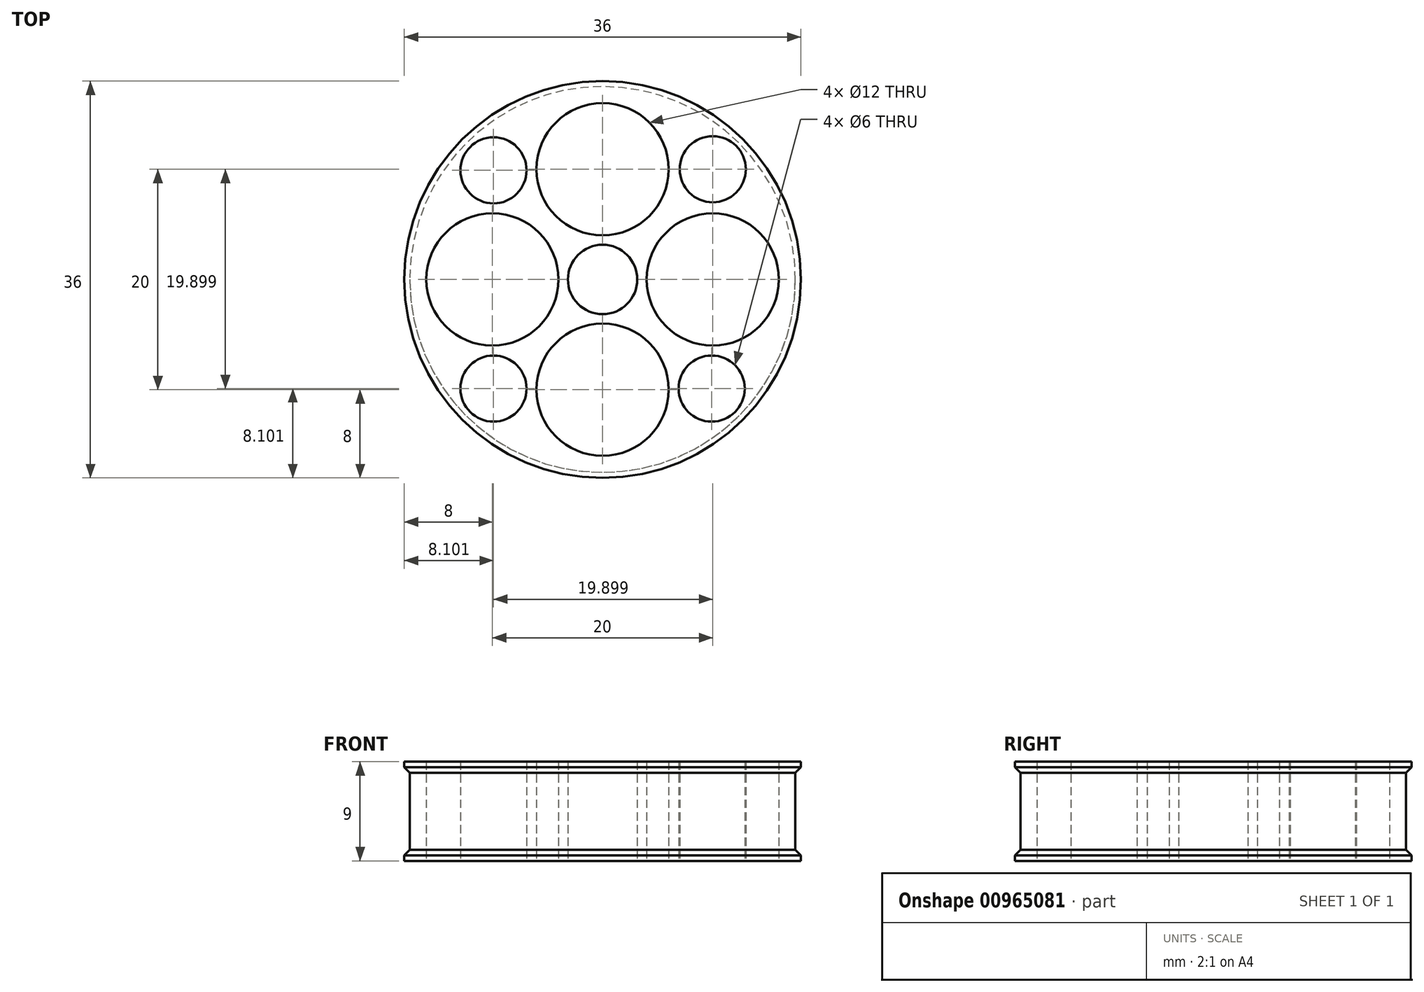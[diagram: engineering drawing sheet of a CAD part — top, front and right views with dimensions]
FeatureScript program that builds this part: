
annotation { "Feature Type Name" : "Feature", "Feature Type Description" : "" }
export const myFeature = defineFeature(function(context is Context, id is Id, definition is map)
    precondition{}
    {
        {
            var Q0;
            Q0=qCreatedBy(makeId("Top.planeOp"),FACE);
            var sketch = newSketch(context, id + "F0", { "sketchPlane" : qUnion([Q0])});
            skCircle(sketch, "E0", {"center": v(0, 0) * mm, "radius": 17.5 * mm});
            skCircle(sketch, "E1", {"center": v(0, 0) * mm, "radius": 3.15 * mm});
            skCircle(sketch, "E2", {"center": v(0, 10) * mm, "radius": 6 * mm});
            skCircle(sketch, "E3", {"center": v(10, 0) * mm, "radius": 6 * mm});
            skCircle(sketch, "E4", {"center": v(0, -10) * mm, "radius": 6 * mm});
            skCircle(sketch, "E5", {"center": v(-10, 0) * mm, "radius": 6 * mm});
            skLineSegment(sketch, "E6", {"start": v(-15.8, 15.8) * mm, "end": v(19.1, -19.1) * mm, "construction": true});
            skLineSegment(sketch, "E7", {"start": v(16.46, 16.46) * mm, "end": v(-16.86, -16.86) * mm, "construction": true});
            skCircle(sketch, "E8", {"center": v(9.9, -9.9) * mm, "radius": 3 * mm});
            skCircle(sketch, "E9", {"center": v(-9.9, -9.9) * mm, "radius": 3 * mm});
            skCircle(sketch, "E10", {"center": v(10, 10) * mm, "radius": 3 * mm});
            skCircle(sketch, "E11", {"center": v(-9.9, 9.9) * mm, "radius": 3 * mm});
            skSolve(sketch);
        }
        {
            var Q0;
            Q0=makeQuery(id+"F0.imprint","IMPRINT",FACE,{"disambiguationData":[TD([[makeQuery(id+"F0.imprint","IMPRINT",EDGE,{"derivedFrom":sQuery(id+"F0.wireOp",EDGE,"E0")}),1.0]])]});
            extrude(context, id + "F1", {"entities" : qUnion([Q0]), "depth" : 7 * mm, "offsetDistance" : 25 * mm});
        }
        {
            var Q0;
            Q0=makeQuery(id+"F1.opExtrude","CAP_FACE",FACE,{"disambiguationData":[OSD([sQuery(id+"F0.wireOp",EDGE,"E0"),sQuery(id+"F0.wireOp",EDGE,"E1"),sQuery(id+"F0.wireOp",EDGE,"E2"),sQuery(id+"F0.wireOp",EDGE,"E3"),sQuery(id+"F0.wireOp",EDGE,"E4"),sQuery(id+"F0.wireOp",EDGE,"E5")])],"isStart":false});
            var sketch = newSketch(context, id + "F2", { "sketchPlane" : qUnion([Q0])});
            skCircle(sketch, "E12", {"center": v(0, 0) * mm, "radius": 18 * mm});
            skSolve(sketch);
        }
        {
            var Q0;
            Q0=makeQuery(id+"F2.imprint","IMPRINT",FACE,{"disambiguationData":[TD([[makeQuery(id+"F2.imprint","IMPRINT",EDGE,{"derivedFrom":sQuery(id+"F2.wireOp",EDGE,"E12")}),1.0]])]});
            var Q1;
            Q1=makeQuery(id+"F2.imprint","IMPRINT",FACE,{"disambiguationData":[TD([[makeQuery(id+"F2.imprint","IMPRINT",EDGE,{"derivedFrom":makeQuery(id+"F1.opExtrude","CAP_EDGE",EDGE,{"disambiguationData":[OSD([sQuery(id+"F0.wireOp",EDGE,"E0")])],"isStart":false})}),1.0]])]});
            extrude(context, id + "F3", {"entities" : qUnion([Q0, Q1]), "operationType" : NewBodyOperationType.ADD, "depth" : 1 * mm, "offsetDistance" : 25 * mm});
        }
        {
            var Q0;
            Q0=makeQuery(id+"F1.opExtrude","CAP_FACE",FACE,{"disambiguationData":[OSD([sQuery(id+"F0.wireOp",EDGE,"E0"),sQuery(id+"F0.wireOp",EDGE,"E1"),sQuery(id+"F0.wireOp",EDGE,"E2"),sQuery(id+"F0.wireOp",EDGE,"E3"),sQuery(id+"F0.wireOp",EDGE,"E4"),sQuery(id+"F0.wireOp",EDGE,"E5")])],"isStart":true});
            var sketch = newSketch(context, id + "F4", { "sketchPlane" : qUnion([Q0])});
            skCircle(sketch, "E13", {"center": v(0, 0) * mm, "radius": 18 * mm});
            skSolve(sketch);
        }
        {
            var Q0;
            Q0=makeQuery(id+"F4.imprint","IMPRINT",FACE,{"disambiguationData":[TD([[makeQuery(id+"F4.imprint","IMPRINT",EDGE,{"derivedFrom":sQuery(id+"F4.wireOp",EDGE,"E13")}),1.0]])]});
            var Q1;
            Q1=makeQuery(id+"F4.imprint","IMPRINT",FACE,{"disambiguationData":[TD([[makeQuery(id+"F4.imprint","IMPRINT",EDGE,{"derivedFrom":makeQuery(id+"F1.opExtrude","CAP_EDGE",EDGE,{"disambiguationData":[OSD([sQuery(id+"F0.wireOp",EDGE,"E0")])],"isStart":true})}),-1.0]])]});
            extrude(context, id + "F5", {"entities" : qUnion([Q0, Q1]), "operationType" : NewBodyOperationType.ADD, "depth" : 1 * mm, "offsetDistance" : 25 * mm});
        }
        {
            var Q0;
            Q0=makeQuery(id+"F5.opExtrude","CAP_EDGE",EDGE,{"disambiguationData":[OSD([sQuery(id+"F4.wireOp",EDGE,"E13")])],"isStart":true});
            var Q1;
            Q1=makeQuery(id+"F3.opExtrude","CAP_EDGE",EDGE,{"disambiguationData":[OSD([sQuery(id+"F2.wireOp",EDGE,"E12")])],"isStart":true});
            chamfer(context, id + "F6", {"entities" : qUnion([Q0, Q1]), "width" : 0.5 * mm, "tangentPropagation" : true});
        }
    });
